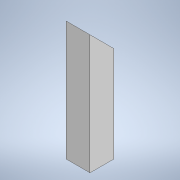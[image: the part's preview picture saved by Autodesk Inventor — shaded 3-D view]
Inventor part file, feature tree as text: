
AUTODESK INVENTOR PART (.ipt)
format: ipt  version: 2022 (Build 260153000, 153)  size: 99,840 bytes
history: native  units: mm
features: extrude x2, sketch x2
ambient origin geometry x8: Origin, YZ Plane, XZ Plane, XY Plane, X Axis, Y Axis, Z Axis, Center Point
bodies: Solid1 (feature_tree)
feature tree (4):
  extrude  "Extrusion1"  Depth=2.0mm
  extrude  "Extrusion2"  TaperAngle=45.0deg  [1 undecoded]
  sketch  "Sketch2"  dims[d5=2.0mm d6=2.0mm]
  sketch  "Sketch3"  dims[d7=10.0mm d8=0.0mm d9=45.0deg d10=0.0mm d11=0.0mm]
note: 1 required parameter value undecoded (feature->parameter linkage not recoverable at this tier; creation-order binding heuristic only, values carry confidence <= 0.55)
